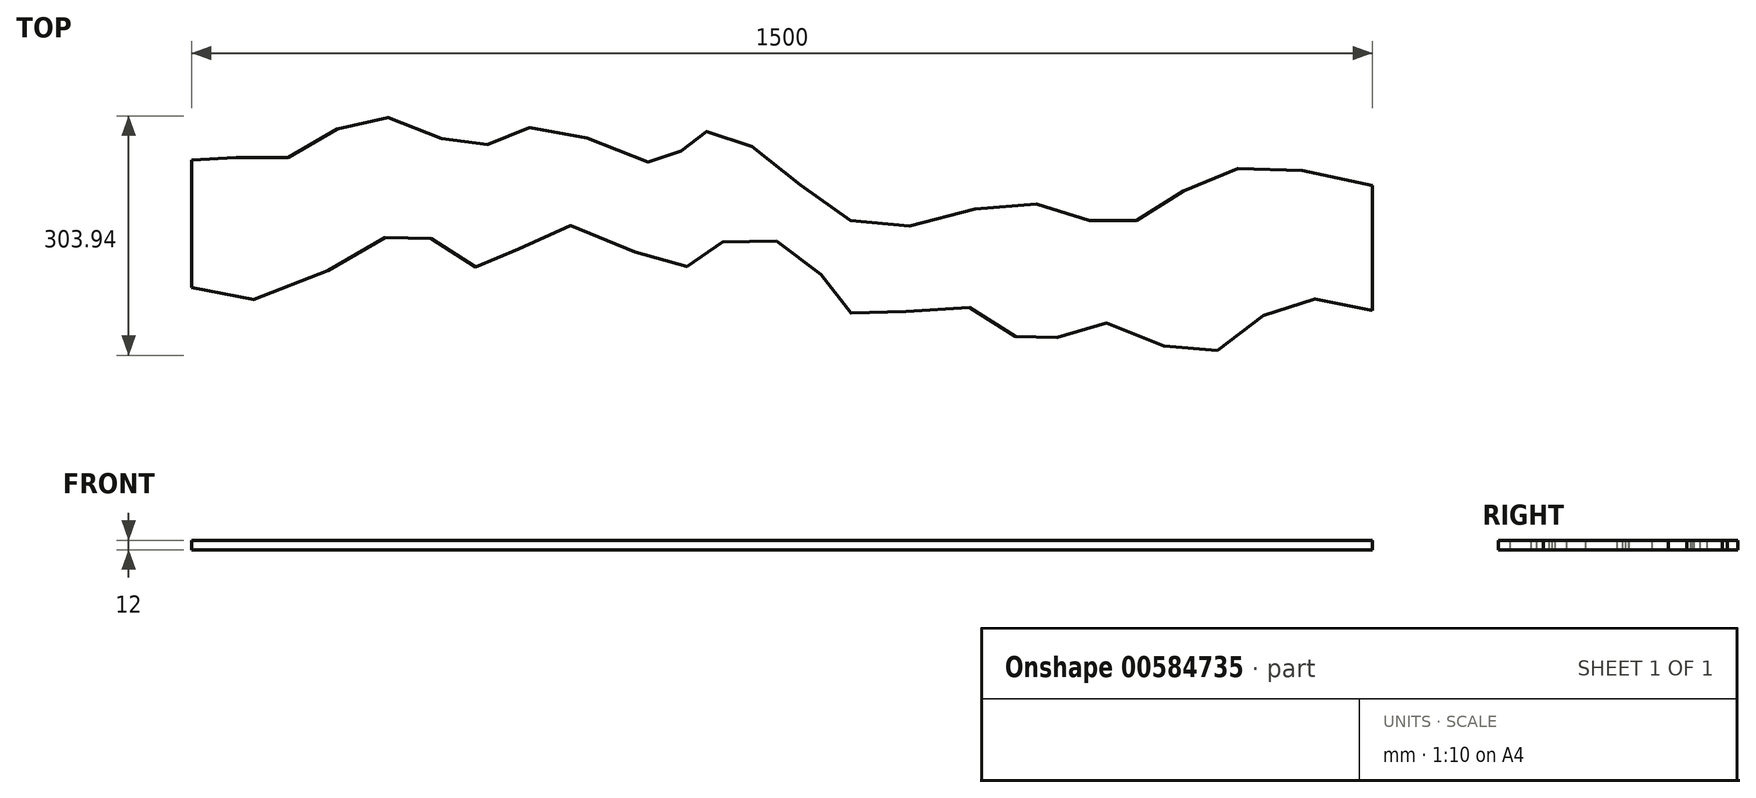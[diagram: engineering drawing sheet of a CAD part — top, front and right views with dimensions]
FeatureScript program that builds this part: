
annotation { "Feature Type Name" : "Feature", "Feature Type Description" : "" }
export const myFeature = defineFeature(function(context is Context, id is Id, definition is map)
    precondition{}
    {
        {
            var Q0;
            Q0=qCreatedBy(makeId("Top.planeOp"),FACE);
            var sketch = newSketch(context, id + "F0", { "sketchPlane" : qUnion([Q0])});
            skPoint(sketch, "E0.14.internal.snap0", {"position": v(-1143.05, 178.12) * mm});
            skPoint(sketch, "E0.16.internal.snap0", {"position": v(-1143.05, 178.12) * mm});
            skPoint(sketch, "E0.18.internal.snap0", {"position": v(-1143.05, 178.12) * mm});
            skFitSpline(sketch, "E0", {"points": [v(356.95, 283.44) * mm, v(158.1, 297.67) * mm, v(36.07, 233.18) * mm, v(-89.92, 262.08) * mm, v(-277.23, 229.66) * mm, v(-417.5, 323.93) * mm, v(-504.76, 347.32) * mm, v(-540.53, 311.54) * mm, v(-697.25, 358.4) * mm, v(-785.72, 331.89) * mm, v(-914.52, 371.26) * mm, v(-1038.41, 313.74) * mm, v(-1143.05, 315.75) * mm, v(-1143.05, 153.42) * mm, v(-964.53, 178.12) * mm, v(-854.9, 223.2) * mm, v(-769.63, 178.12) * mm, v(-674.6, 232.18) * mm, v(-526.44, 178.12) * mm, v(-468.18, 211.63) * mm, v(-360.8, 191.21) * mm, v(-299.95, 118.44) * mm, v(-161.02, 129.57) * mm, v(-73.67, 82.22) * mm, v(11.47, 108.8) * mm, v(138.6, 67.61) * mm, v(238.55, 130.96) * mm, v(356.95, 124.6) * mm], "startDerivative": vector(-4535.7, 1100.87) * mm, "endDerivative": vector(3438.34, -939.7) * mm});
            skFitSpline(sketch, "E1", {"points": [v(356.95, 124.6) * mm, v(356.95, 283.44) * mm], "startDerivative": vector(0, 158.83) * mm, "endDerivative": vector(0, 158.83) * mm});
            skFitSpline(sketch, "E2", {"points": [v(-1143.05, 153.42) * mm, v(-1143.05, 315.75) * mm], "startDerivative": vector(0, 162.33) * mm, "endDerivative": vector(0, 162.33) * mm});
            skFitSpline(sketch, "E3", {"points": [v(-1168.09, 229.66) * mm, v(-1168.1, 240.98) * mm], "startDerivative": vector(0.11, 11.32) * mm, "endDerivative": vector(0.11, 11.32) * mm});
            skPoint(sketch, "E4.14.internal.snap0", {"position": v(45, -188.87) * mm});
            skPoint(sketch, "E4.16.internal.snap0", {"position": v(45, -188.87) * mm});
            skPoint(sketch, "E4.18.internal.snap0", {"position": v(45, -188.87) * mm});
            skFitSpline(sketch, "E4", {"points": [v(1545, -83.55) * mm, v(1346.14, -69.32) * mm, v(1224.12, -133.8) * mm, v(1098.13, -104.9) * mm, v(910.81, -137.33) * mm, v(770.54, -43.05) * mm, v(683.29, -19.67) * mm, v(647.52, -55.44) * mm, v(490.8, -8.59) * mm, v(402.33, -35.1) * mm, v(273.53, 4.27) * mm, v(149.64, -53.24) * mm, v(45, -51.24) * mm, v(45, -213.56) * mm, v(223.52, -188.87) * mm, v(333.14, -143.8) * mm, v(418.42, -188.87) * mm, v(513.44, -134.8) * mm, v(661.61, -188.87) * mm, v(719.87, -155.36) * mm, v(827.26, -175.78) * mm, v(888.1, -248.55) * mm, v(1027.03, -237.41) * mm, v(1114.38, -284.76) * mm, v(1199.51, -258.18) * mm, v(1326.65, -299.37) * mm, v(1426.6, -236.03) * mm, v(1545, -242.38) * mm], "startDerivative": vector(-4535.7, 1100.87) * mm, "endDerivative": vector(3438.34, -939.7) * mm});
            skFitSpline(sketch, "E5", {"points": [v(1545, -242.38) * mm, v(1545, -83.55) * mm], "startDerivative": vector(0, 158.83) * mm, "endDerivative": vector(0, 158.83) * mm});
            skFitSpline(sketch, "E6", {"points": [v(45, -213.56) * mm, v(45, -51.24) * mm], "startDerivative": vector(0, 162.33) * mm, "endDerivative": vector(0, 162.33) * mm});
            skFitSpline(sketch, "E7", {"points": [v(19.96, -137.33) * mm, v(19.95, -126) * mm], "startDerivative": vector(0.11, 11.32) * mm, "endDerivative": vector(0.11, 11.32) * mm});
            skSolve(sketch);
        }
        {
            var Q0;
            {var subQ0=sQuery(id+"F0.wireOp",EDGE,"E1");Q0=makeQuery(id+"F0.imprint","IMPRINT",FACE,{"disambiguationData":[TD([[makeQuery(id+"F0.imprint","IMPRINT",EDGE,{"derivedFrom":subQ0}),1.0]])]});}
            extrude(context, id + "F1", {"entities" : qUnion([Q0]), "depth" : 12 * mm, "offsetDistance" : 25 * mm});
        }
    });
